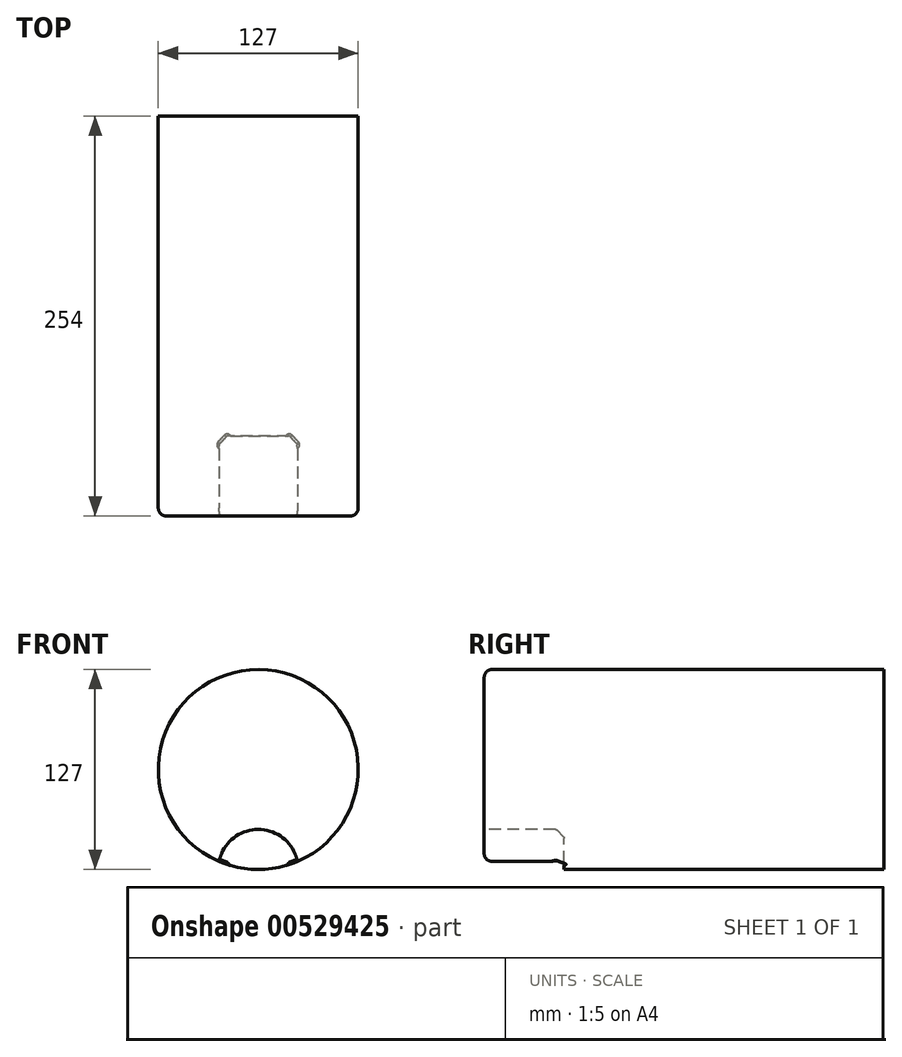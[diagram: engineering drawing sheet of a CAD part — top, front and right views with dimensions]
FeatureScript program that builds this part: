
annotation { "Feature Type Name" : "Feature", "Feature Type Description" : "" }
export const myFeature = defineFeature(function(context is Context, id is Id, definition is map)
    precondition{}
    {
        {
            var Q0;
            Q0=qCreatedBy(makeId("Front.planeOp"),FACE);
            var sketch = newSketch(context, id + "F0", { "sketchPlane" : qUnion([Q0])});
            skCircle(sketch, "E0", {"center": v(0, 0) * mm, "radius": 63.5 * mm});
            skSolve(sketch);
        }
        {
            var Q0;
            Q0=makeQuery(id+"F0.imprint","IMPRINT",FACE,{"disambiguationData":[TD([[makeQuery(id+"F0.imprint","IMPRINT",EDGE,{"derivedFrom":sQuery(id+"F0.wireOp",EDGE,"E0")}),1.0]])]});
            extrude(context, id + "F1", {"entities" : qUnion([Q0]), "depth" : 254 * mm, "offsetDistance" : 25.4 * mm});
        }
        {
            var Q0;
            Q0=makeQuery(id+"F1.opExtrude","CAP_FACE",FACE,{"disambiguationData":[OSD([sQuery(id+"F0.wireOp",EDGE,"E0")])],"isStart":false});
            var sketch = newSketch(context, id + "F2", { "sketchPlane" : qUnion([Q0])});
            skCircle(sketch, "E1", {"center": v(0, -63.5) * mm, "radius": 25.4 * mm});
            skSolve(sketch);
        }
        {
            var Q0;
            {var subQ0=sQuery(id+"F2.wireOp",EDGE,"E1");var subQ1=makeQuery(id+"F1.opExtrude","CAP_EDGE",EDGE,{"disambiguationData":[OSD([sQuery(id+"F0.wireOp",EDGE,"E0")])],"isStart":false});var subQ2=makeQuery(id+"F2.imprint","INTERSECT",VERTEX,{"disambiguationData":[OD(0.0)],"derivedFrom":[subQ1,subQ0]});Q0=makeQuery(id+"F2.imprint","IMPRINT",FACE,{"disambiguationData":[TD([[makeQuery(id+"F2.imprint","IMPRINT",EDGE,{"disambiguationData":[TD([[subQ2,1.0]])],"derivedFrom":subQ0}),1.0]])]});}
            extrude(context, id + "F3", {"entities" : qUnion([Q0]), "operationType" : NewBodyOperationType.REMOVE, "oppositeDirection" : true, "depth" : 50.8 * mm, "offsetDistance" : 25.4 * mm});
        }
        {
            var Q0;
            Q0=makeQuery(id+"F1.opExtrude","CAP_EDGE",EDGE,{"disambiguationData":[OSD([sQuery(id+"F0.wireOp",EDGE,"E0")])],"isStart":false});
            fillet(context, id + "F4", {"entities" : qUnion([Q0]), "radius" : 5.08 * mm, "tangentPropagation" : true, "allowEdgeOverflow" : false});
        }
        {
            var Q0;
            Q0=makeQuery(id+"F3.boolean.opBoolean","COPY",EDGE,{"derivedFrom":makeQuery(id+"F3.opExtrude","CAP_EDGE",EDGE,{"disambiguationData":[OSD([sQuery(id+"F2.wireOp",EDGE,"E1")])],"isStart":false})});
            chamfer(context, id + "F5", {"entities" : qUnion([Q0]), "width" : 5.08 * mm, "tangentPropagation" : true});
        }
        {
            var Q0;
            {var subQ0=sQuery(id+"F2.wireOp",EDGE,"E1");var subQ1=sQuery(id+"F0.wireOp",EDGE,"E0");Q0=makeQuery(id+"F3.boolean.opBoolean","COPY",EDGE,{"derivedFrom":makeQuery(id+"F3.opExtrude","SWEPT_EDGE",EDGE,{"disambiguationData":[OSD([subQ1,subQ0]),TDD([makeQuery(id+"F2.imprint","INTERSECT",VERTEX,{"disambiguationData":[OD(0.0)],"derivedFrom":[makeQuery(id+"F1.opExtrude","CAP_EDGE",EDGE,{"disambiguationData":[OSD([subQ1])],"isStart":false}),subQ0]})])]})});}
            var Q1;
            Q1=makeQuery(id+"F3.boolean.opBoolean","COPY",EDGE,{"derivedFrom":makeQuery(id+"F3.opExtrude","CAP_EDGE",EDGE,{"disambiguationData":[OSD([sQuery(id+"F0.wireOp",EDGE,"E0")])],"isStart":false})});
            var Q2;
            Q2=makeQuery(id+"F5.opChamfer","BLEND_EDGE",EDGE,{"disambiguationData":[OD(0.0)],"blendedFrom":[makeQuery(id+"F3.boolean.opBoolean","COPY",EDGE,{"derivedFrom":makeQuery(id+"F3.opExtrude","CAP_EDGE",EDGE,{"disambiguationData":[OSD([sQuery(id+"F2.wireOp",EDGE,"E1")])],"isStart":false})}),makeQuery(id+"F1.opExtrude","SWEPT_FACE",FACE,{"disambiguationData":[OSD([sQuery(id+"F0.wireOp",EDGE,"E0")])]})],"blendedInto":[makeQuery(id+"F1.opExtrude","SWEPT_FACE",FACE,{"disambiguationData":[OSD([sQuery(id+"F0.wireOp",EDGE,"E0")])]})]});
            var Q3;
            Q3=makeQuery(id+"F5.opChamfer","BLEND_EDGE",EDGE,{"disambiguationData":[OD(1.0)],"blendedFrom":[makeQuery(id+"F3.boolean.opBoolean","COPY",EDGE,{"derivedFrom":makeQuery(id+"F3.opExtrude","CAP_EDGE",EDGE,{"disambiguationData":[OSD([sQuery(id+"F2.wireOp",EDGE,"E1")])],"isStart":false})}),makeQuery(id+"F1.opExtrude","SWEPT_FACE",FACE,{"disambiguationData":[OSD([sQuery(id+"F0.wireOp",EDGE,"E0")])]})],"blendedInto":[makeQuery(id+"F1.opExtrude","SWEPT_FACE",FACE,{"disambiguationData":[OSD([sQuery(id+"F0.wireOp",EDGE,"E0")])]})]});
            var Q4;
            {var subQ0=sQuery(id+"F2.wireOp",EDGE,"E1");Q4=makeQuery(id+"F5.opChamfer","BLEND_EDGE",EDGE,{"blendedFrom":[makeQuery(id+"F3.boolean.opBoolean","COPY",EDGE,{"derivedFrom":makeQuery(id+"F3.opExtrude","CAP_EDGE",EDGE,{"disambiguationData":[OSD([subQ0])],"isStart":false})}),makeQuery(id+"F3.boolean.opBoolean","COPY",FACE,{"derivedFrom":makeQuery(id+"F3.opExtrude","CAP_FACE",FACE,{"disambiguationData":[OSD([sQuery(id+"F0.wireOp",EDGE,"E0"),subQ0])],"isStart":false})})],"blendedInto":[makeQuery(id+"F3.boolean.opBoolean","COPY",FACE,{"derivedFrom":makeQuery(id+"F3.opExtrude","CAP_FACE",FACE,{"disambiguationData":[OSD([sQuery(id+"F0.wireOp",EDGE,"E0"),subQ0])],"isStart":false})})]});}
            var Q5;
            {var subQ0=sQuery(id+"F2.wireOp",EDGE,"E1");Q5=makeQuery(id+"F5.opChamfer","BLEND_EDGE",EDGE,{"blendedFrom":[makeQuery(id+"F3.boolean.opBoolean","COPY",EDGE,{"derivedFrom":makeQuery(id+"F3.opExtrude","CAP_EDGE",EDGE,{"disambiguationData":[OSD([subQ0])],"isStart":false})}),makeQuery(id+"F3.boolean.opBoolean","COPY",FACE,{"derivedFrom":makeQuery(id+"F3.opExtrude","SWEPT_FACE",FACE,{"disambiguationData":[OSD([subQ0])]})})],"blendedInto":[makeQuery(id+"F3.boolean.opBoolean","COPY",FACE,{"derivedFrom":makeQuery(id+"F3.opExtrude","SWEPT_FACE",FACE,{"disambiguationData":[OSD([subQ0])]})})]});}
            fillet(context, id + "F6", {"entities" : qUnion([Q0, Q1, Q2, Q3, Q4, Q5]), "radius" : 1.27 * mm, "tangentPropagation" : true, "allowEdgeOverflow" : false});
        }
    });
